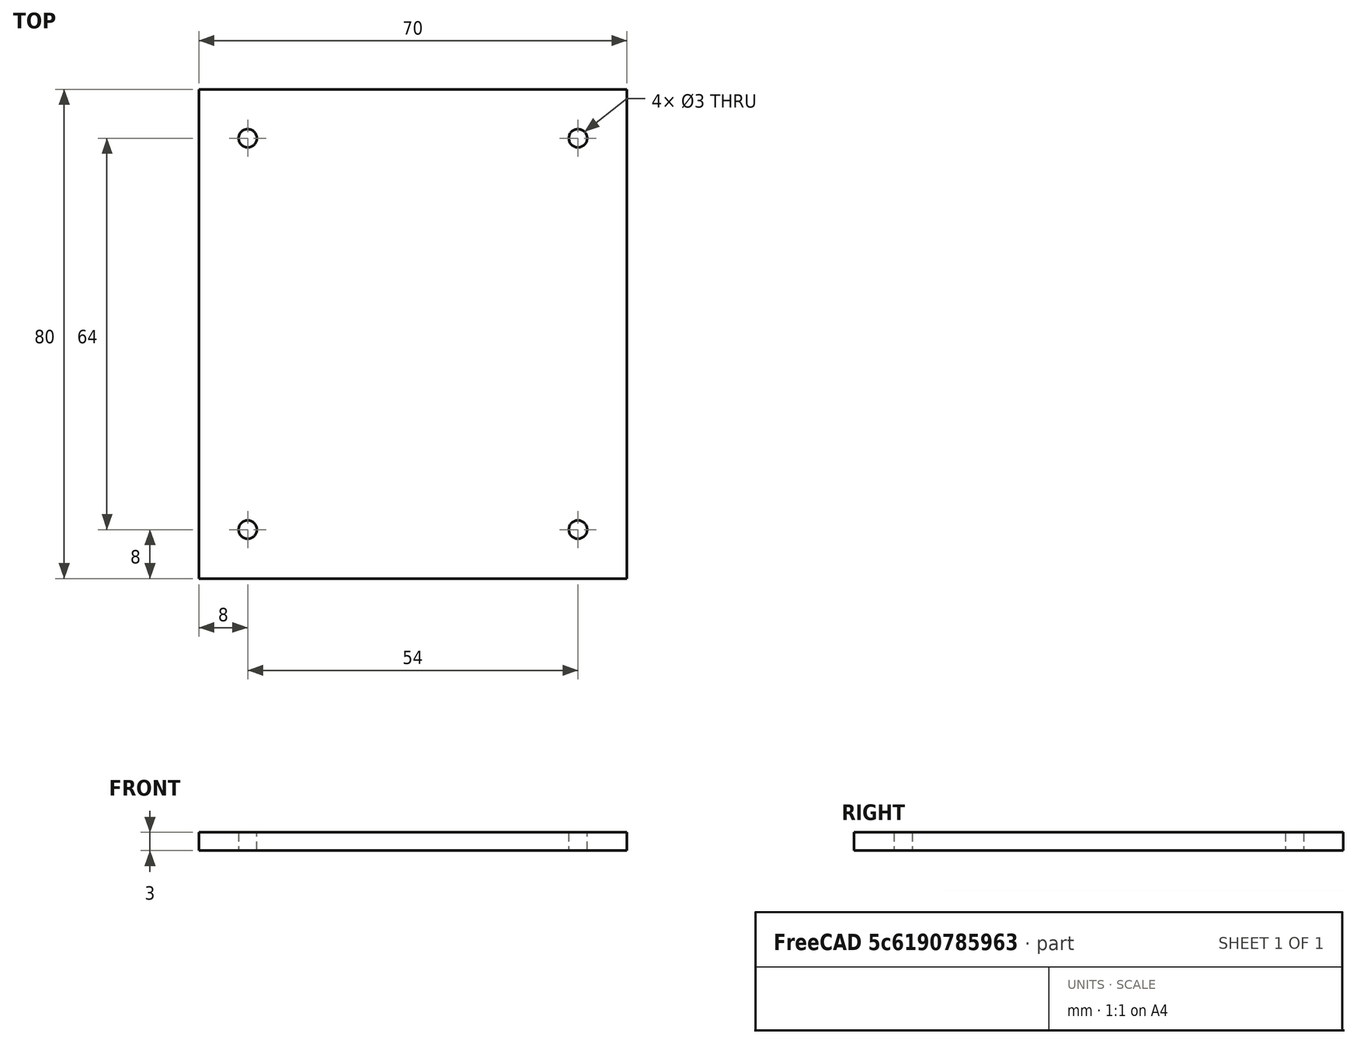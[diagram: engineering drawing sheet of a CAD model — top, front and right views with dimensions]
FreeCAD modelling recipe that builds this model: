
FCSTD DOCUMENT  (FreeCAD 0.17R13522 (Git))
Label: Tampa
License: All rights reserved
LicenseURL: http://en.wikipedia.org/wiki/All_rights_reserved
objects: App::Part×1, Sketcher::SketchObject×1, PartDesign::Pad×1, PartDesign::Body×1
note: 4 computed .brp shape members not serialized (recipe doc carries the construction recipe); baked Part::Feature solids carry a one-line shape summary decoded from their .brp

FEATURE [App::Part] Part
  License = CC BY 3.0
  LicenseURL = http://creativecommons.org/licenses/by/3.0/
  Origin = -> Origin
FEATURE [Sketcher::SketchObject] Sketch
  MapMode = 5
  Support = -> [XY_Plane001]
  sketch-geometry (12):
    g0: LineSegment StartX=-35 StartY=40 StartZ=0 EndX=35 EndY=40 EndZ=0
    g1: LineSegment StartX=35 StartY=40 StartZ=0 EndX=35 EndY=-40 EndZ=0
    g2: LineSegment StartX=35 StartY=-40 StartZ=0 EndX=-35 EndY=-40 EndZ=0
    g3: LineSegment StartX=-35 StartY=-40 StartZ=0 EndX=-35 EndY=40 EndZ=0
    g4: Circle CenterX=-27 CenterY=32 CenterZ=0 NormalX=0 NormalY=0 NormalZ=1 AngleXU=0 Radius=1.5
    g5: Circle CenterX=27 CenterY=32 CenterZ=0 NormalX=0 NormalY=0 NormalZ=1 AngleXU=0 Radius=1.5
    g6: Circle CenterX=27 CenterY=-32 CenterZ=0 NormalX=0 NormalY=0 NormalZ=1 AngleXU=0 Radius=1.5
    g7: Circle CenterX=-27 CenterY=-32 CenterZ=0 NormalX=0 NormalY=0 NormalZ=1 AngleXU=0 Radius=1.5
    g8: LineSegment [constr] StartX=-27 StartY=32 StartZ=0 EndX=27 EndY=32 EndZ=0
    g9: LineSegment [constr] StartX=27 StartY=32 StartZ=0 EndX=27 EndY=-32 EndZ=0
    g10: LineSegment [constr] StartX=27 StartY=-32 StartZ=0 EndX=-27 EndY=-32 EndZ=0
    g11: LineSegment [constr] StartX=-27 StartY=-32 StartZ=0 EndX=-27 EndY=32 EndZ=0
  constraints (31):
    c: Coincident(g0,g1)
    c: Coincident(g1,g2)
    c: Coincident(g2,g3)
    c: Coincident(g3,g0)
    c: Horizontal(g0)
    c: Horizontal(g2)
    c: Vertical(g1)
    c: Vertical(g3)
    c: DistanceX(g0,g0) = 70
    c: DistanceY(g1,g1) = 80
    c: Symmetric(g2,g0,g-1)
    c: Radius(g4) = 1.5
    c: Equal(g4,g5)
    c: Equal(g4,g6)
    c: Equal(g4,g7)
    c: Coincident(g8,g9)
    c: Coincident(g9,g10)
    c: Coincident(g10,g11)
    c: Coincident(g11,g8)
    c: Horizontal(g8)
    c: Horizontal(g10)
    c: Vertical(g9)
    c: Vertical(g11)
    c: DistanceX(g8,g0) = 8
    c: DistanceY(g8,g0) = 8
    c: DistanceX(g2,g10) = 8
    c: DistanceY(g2,g10) = 8
    c: Coincident(g4,g8)
    c: Coincident(g5,g8)
    c: Coincident(g9,g6)
    c: Coincident(g10,g7)
FEATURE [PartDesign::Pad] Pad
  Length = 3
  Length2 = 100
  Profile = -> Sketch
  Type = 0
FEATURE [PartDesign::Body] Body
  Group = -> [Sketch,Pad]
  Origin = -> Origin001
  Tip = -> Pad
